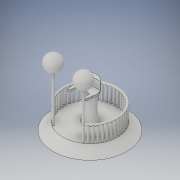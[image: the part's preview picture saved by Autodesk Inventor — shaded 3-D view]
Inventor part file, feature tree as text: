
AUTODESK INVENTOR PART (.ipt)
format: ipt  version: 2017 (Build 210142000, 142)  size: 727,552 bytes
history: native  units: in
note: dims shown in document units (in); Inventor stores cm internally (conversion verified against a paired STEP export)
features: other x20, sketch x8, extrude x5, loft x1, fillet x1
ambient origin geometry x7: Origin, YZ Plane, XY Plane, X Axis, Y Axis, Z Axis, Center Point
bodies: Body1 (feature_tree)
feature tree (35):
  other  "bace + terminal"
  other  "bace of terminal"
  other  "middle workplane"
  other  "middle"
  other  "top workplane"
  loft  "curved tower"
  extrude  "arm rests and terminal monitor"  Depth=0.8in
  other  "middle of the part vertical"
  other  "used to line up the key board and mouse"
  extrude  "bace"  Depth=1.8247in
  other  "ramp around"
  extrude  "railing bars"  Depth=1.0in
  other  "railing bar top workplane"
  other  "railing bar top"
  extrude  "light pole"  Depth=1.2in
  other  "globe light workplane"
  sketch  "Sketch20"  dims[d20=0.85in d27=1.1in d28=0.75in]
  other  "light 1"
  other  "light 2"
  other  "mate to back to monitor"
  extrude  "monitor raise"  Depth=1.1in
  fillet  "curve edges"  Radius=0.75in
  other  "bottom workplane"
  other  "top"
  sketch  "Sketch15"  dims[d0=1.0in d1=0.75in]
  sketch  "Sketch16"  dims[d2=1.8247in d3=0.8in]
  sketch  "Sketch17"  dims[d4=0.55in d5=1.8247in]
  other  "Work Axis3"
  other  "Work Axis4"
  sketch  "Sketch18"  dims[d6=0.75in d7=1.0in]
  sketch  "Sketch19"  dims[d8=0.0in d9=90.0deg d10=0.0in d11=90.0deg d12=0.0in d13=90.0deg d19=1.2in]
  other  "Work Axis5"
  other  "Work Axis6"
  sketch  "Sketch23"  dims[d29=1.0in]
  sketch  "Sketch25"  dims[d30=0.65in d42=1.1in d43=0.85in d44=1.0in d45=0.75in d49=1.2in d50=0.85in d51=1.0in d52=0.75in d122=7.0in d123=1.0in d124=0.0in d134=0.7579in d135=15.748in d137=1.9948in d139=2.0in d140=0.0in d141=0.2749in d142=90.0deg d143=0.25in d144=0.25in d145=90.0deg d146=4.0in d147=0.0in d150=2.0in d151=0.9in d152=2.0in d153=0.9in d155=90.0deg d156=90.0deg d163=0.8125in d165=0.4167in d166=0.8125in d167=0.4167in d168=0.2083in d169=0.0in d170=1.125in d173=1.8892in d174=1.1844in d175=1.125in d176=1.125in d177=1.1844in d178=1.0in d179=0.0in d180=0.5527in d181=0.01in]
